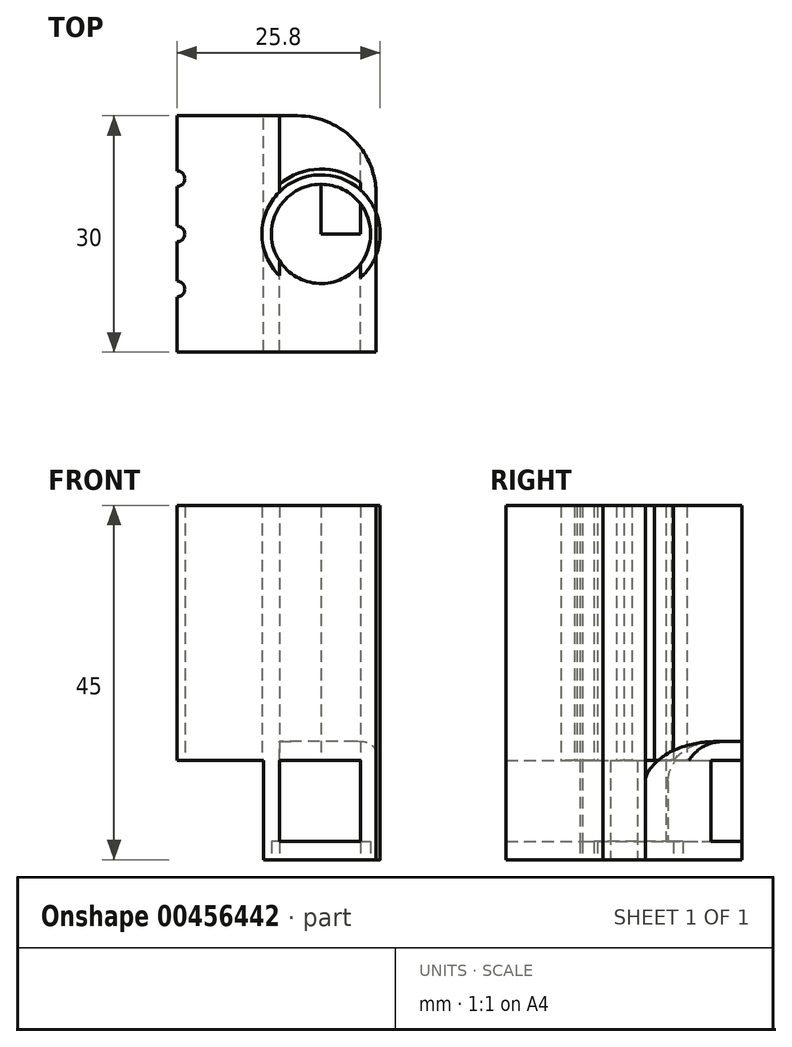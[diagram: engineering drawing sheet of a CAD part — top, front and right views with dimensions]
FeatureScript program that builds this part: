
annotation { "Feature Type Name" : "Feature", "Feature Type Description" : "" }
export const myFeature = defineFeature(function(context is Context, id is Id, definition is map)
    precondition{}
    {
        {
            var Q0;
            Q0=qCreatedBy(makeId("Top.planeOp"),FACE);
            var sketch = newSketch(context, id + "F0", { "sketchPlane" : qUnion([Q0])});
            skLineSegment(sketch, "E0.bottom", {"start": v(0, 0) * mm, "end": v(37, 0) * mm});
            skLineSegment(sketch, "E0.top", {"start": v(0, -30) * mm, "end": v(37, -30) * mm});
            skLineSegment(sketch, "E0.left", {"start": v(0, 0) * mm, "end": v(0, -30) * mm});
            skLineSegment(sketch, "E0.right", {"start": v(37, 0) * mm, "end": v(37, -30) * mm});
            skLineSegment(sketch, "E1.bottom", {"start": v(37, 0) * mm, "end": v(35, 0) * mm});
            skLineSegment(sketch, "E1.top", {"start": v(37, -30) * mm, "end": v(35, -30) * mm});
            skLineSegment(sketch, "E1.right", {"start": v(35, 0) * mm, "end": v(35, -30) * mm});
            skLineSegment(sketch, "E2.bottom", {"start": v(35, 0) * mm, "end": v(24.7, 0) * mm});
            skLineSegment(sketch, "E2.top", {"start": v(35, -30) * mm, "end": v(24.7, -30) * mm});
            skLineSegment(sketch, "E2.right", {"start": v(24.7, 0) * mm, "end": v(24.7, -30) * mm});
            skLineSegment(sketch, "E3.bottom", {"start": v(24.7, 0) * mm, "end": v(11.7, 0) * mm});
            skLineSegment(sketch, "E3.top", {"start": v(24.7, -30) * mm, "end": v(11.7, -30) * mm});
            skLineSegment(sketch, "E3.right", {"start": v(11.7, 0) * mm, "end": v(11.7, -30) * mm});
            skCircle(sketch, "E4", {"center": v(11.7, -15) * mm, "radius": 1 * mm});
            skCircle(sketch, "E5", {"center": v(11.7, -8) * mm, "radius": 1 * mm});
            skCircle(sketch, "E6", {"center": v(11.7, -22) * mm, "radius": 1 * mm});
            skLineSegment(sketch, "E7.bottom", {"start": v(11.7, 0) * mm, "end": v(6.7, 0) * mm});
            skLineSegment(sketch, "E7.top", {"start": v(11.7, -30) * mm, "end": v(6.7, -30) * mm});
            skLineSegment(sketch, "E7.right", {"start": v(6.7, 0) * mm, "end": v(6.7, -30) * mm});
            skCircle(sketch, "E8.MirrorC", {"center": v(1.7, -8) * mm, "radius": 1 * mm});
            skCircle(sketch, "E9.MirrorC", {"center": v(1.7, -15) * mm, "radius": 1 * mm});
            skCircle(sketch, "E10.MirrorC", {"center": v(1.7, -22) * mm, "radius": 1 * mm});
            skCircle(sketch, "E11", {"center": v(30, -15) * mm, "radius": 7.5 * mm});
            skPoint(sketch, "E11.centerSnap0", {"position": v(24.7, -15) * mm});
            skLineSegment(sketch, "E12.bottom", {"start": v(35, 0) * mm, "end": v(30, 0) * mm});
            skLineSegment(sketch, "E12.top", {"start": v(35, -15) * mm, "end": v(30, -15) * mm});
            skLineSegment(sketch, "E12.left", {"start": v(35, 0) * mm, "end": v(35, -15) * mm});
            skLineSegment(sketch, "E12.right", {"start": v(30, 0) * mm, "end": v(30, -15) * mm});
            skCircle(sketch, "E13", {"center": v(30, -15) * mm, "radius": 6.3 * mm});
            skSolve(sketch);
        }
        {
            var Q0;
            {var subQ0=sQuery(id+"F0.wireOp",EDGE,"E1.bottom");Q0=makeQuery(id+"F0.imprint","IMPRINT",FACE,{"disambiguationData":[TD([[makeQuery(id+"F0.imprint","IMPRINT",EDGE,{"derivedFrom":subQ0}),1.0]])]});}
            var Q1;
            {var subQ0=sQuery(id+"F0.wireOp",EDGE,"E1.top");Q1=makeQuery(id+"F0.imprint","IMPRINT",FACE,{"disambiguationData":[TD([[makeQuery(id+"F0.imprint","IMPRINT",EDGE,{"derivedFrom":subQ0}),-1.0]])]});}
            var Q2;
            {var subQ0=sQuery(id+"F0.wireOp",EDGE,"E2.bottom");Q2=makeQuery(id+"F0.imprint","IMPRINT",FACE,{"disambiguationData":[TD([[makeQuery(id+"F0.imprint","IMPRINT",EDGE,{"derivedFrom":subQ0}),1.0]])]});}
            var Q3;
            {var subQ0=sQuery(id+"F0.wireOp",EDGE,"E2.top");Q3=makeQuery(id+"F0.imprint","IMPRINT",FACE,{"disambiguationData":[TD([[makeQuery(id+"F0.imprint","IMPRINT",EDGE,{"derivedFrom":subQ0}),-1.0]])]});}
            var Q4;
            {var subQ5=sQuery(id+"F0.wireOp",EDGE,"E12.bottom");Q4=makeQuery(id+"F0.imprint","IMPRINT",FACE,{"disambiguationData":[TD([[makeQuery(id+"F0.imprint","IMPRINT",EDGE,{"derivedFrom":subQ5}),1.0]])]});}
            var Q5;
            Q5=makeQuery(id+"F0.imprint","IMPRINT",FACE,{"disambiguationData":[TD([[makeQuery(id+"F0.imprint","IMPRINT",EDGE,{"derivedFrom":sQuery(id+"F0.wireOp",EDGE,"E0.bottom")}),-1.0]])]});
            var Q6;
            {var subQ0=sQuery(id+"F0.wireOp",EDGE,"E7.bottom");Q6=makeQuery(id+"F0.imprint","IMPRINT",FACE,{"disambiguationData":[TD([[makeQuery(id+"F0.imprint","IMPRINT",EDGE,{"derivedFrom":subQ0}),1.0]])]});}
            var Q7;
            {var subQ1=sQuery(id+"F0.wireOp",EDGE,"E3.bottom");Q7=makeQuery(id+"F0.imprint","IMPRINT",FACE,{"disambiguationData":[TD([[makeQuery(id+"F0.imprint","IMPRINT",EDGE,{"derivedFrom":subQ1}),1.0]])]});}
            extrude(context, id + "F1", {"entities" : qUnion([Q0, Q1, Q2, Q3, Q4, Q5, Q6, Q7]), "depth" : 15 * mm});
        }
        {
            var Q0;
            {var subQ0=sQuery(id+"F0.wireOp",EDGE,"E12.left");var subQ1=sQuery(id+"F0.wireOp",EDGE,"E11");var subQ2=makeQuery(id+"F0.imprint","INTERSECT",VERTEX,{"derivedFrom":[subQ1,subQ0]});Q0=makeQuery(id+"F0.imprint","IMPRINT",FACE,{"disambiguationData":[TD([[makeQuery(id+"F0.imprint","IMPRINT",EDGE,{"disambiguationData":[TD([[subQ2,-1.0]])],"derivedFrom":subQ1}),1.0]])]});}
            var Q1;
            {var subQ0=sQuery(id+"F0.wireOp",EDGE,"E11");var subQ1=sQuery(id+"F0.wireOp",EDGE,"E2.right");var subQ2=makeQuery(id+"F0.imprint","INTERSECT",VERTEX,{"disambiguationData":[OD(0.0)],"derivedFrom":[subQ1,subQ0]});Q1=makeQuery(id+"F0.imprint","IMPRINT",FACE,{"disambiguationData":[TD([[makeQuery(id+"F0.imprint","IMPRINT",EDGE,{"disambiguationData":[TD([[subQ2,-1.0]])],"derivedFrom":subQ1}),1.0]])]});}
            var Q2;
            {var subQ0=sQuery(id+"F0.wireOp",EDGE,"E11");var subQ1=sQuery(id+"F0.wireOp",EDGE,"E2.right");var subQ2=makeQuery(id+"F0.imprint","INTERSECT",VERTEX,{"disambiguationData":[OD(0.0)],"derivedFrom":[subQ1,subQ0]});Q2=makeQuery(id+"F0.imprint","IMPRINT",FACE,{"disambiguationData":[TD([[makeQuery(id+"F0.imprint","IMPRINT",EDGE,{"disambiguationData":[TD([[subQ2,-1.0]])],"derivedFrom":subQ1}),-1.0]])]});}
            var Q3;
            {var subQ0=sQuery(id+"F0.wireOp",EDGE,"E13");var subQ1=sQuery(id+"F0.wireOp",EDGE,"E1.right");var subQ2=makeQuery(id+"F0.imprint","INTERSECT",VERTEX,{"derivedFrom":[subQ1,subQ0]});Q3=makeQuery(id+"F0.imprint","IMPRINT",FACE,{"disambiguationData":[TD([[makeQuery(id+"F0.imprint","IMPRINT",EDGE,{"disambiguationData":[TD([[subQ2,-1.0]])],"derivedFrom":subQ1}),-1.0]])]});}
            var Q4;
            {var subQ0=sQuery(id+"F0.wireOp",EDGE,"E11");var subQ1=sQuery(id+"F0.wireOp",EDGE,"E0.right");var subQ7=makeQuery(id+"F0.imprint","INTERSECT",VERTEX,{"disambiguationData":[OD(0.0)],"derivedFrom":[subQ1,subQ0]});Q4=makeQuery(id+"F0.imprint","IMPRINT",FACE,{"disambiguationData":[TD([[makeQuery(id+"F0.imprint","IMPRINT",EDGE,{"disambiguationData":[TD([[subQ7,-1.0]])],"derivedFrom":subQ1}),-1.0]])]});}
            extrude(context, id + "F2", {"entities" : qUnion([Q0, Q1, Q2, Q3, Q4]), "operationType" : NewBodyOperationType.ADD, "depth" : 45 * mm});
        }
        {
            var Q0;
            Q0=makeQuery(id+"F1.opExtrude","CAP_EDGE",EDGE,{"disambiguationData":[OSD([sQuery(id+"F0.wireOp",EDGE,"E11")])],"isStart":false});
            fillet(context, id + "F3", {"entities" : qUnion([Q0]), "radius" : 5 * mm, "tangentPropagation" : true, "allowEdgeOverflow" : false});
        }
        {
            var Q0;
            Q0=makeQuery(id+"F1.opExtrude","SWEPT_FACE",FACE,{"disambiguationData":[OSD([sQuery(id+"F0.wireOp",EDGE,"E0.bottom"),sQuery(id+"F0.wireOp",EDGE,"E1.bottom"),sQuery(id+"F0.wireOp",EDGE,"E2.bottom"),sQuery(id+"F0.wireOp",EDGE,"E3.bottom"),sQuery(id+"F0.wireOp",EDGE,"E7.bottom"),sQuery(id+"F0.wireOp",EDGE,"E12.bottom")])]});
            var sketch = newSketch(context, id + "F4", { "sketchPlane" : qUnion([Q0])});
            skLineSegment(sketch, "E14.bottom", {"start": v(-37, 15) * mm, "end": v(-35, 15) * mm});
            skLineSegment(sketch, "E14.top", {"start": v(-37, 12.6) * mm, "end": v(-35, 12.6) * mm});
            skLineSegment(sketch, "E14.left", {"start": v(-37, 15) * mm, "end": v(-37, 12.6) * mm});
            skLineSegment(sketch, "E14.right", {"start": v(-35, 15) * mm, "end": v(-35, 12.6) * mm});
            skLineSegment(sketch, "E15.bottom", {"start": v(-35, 12.6) * mm, "end": v(-24.7, 12.6) * mm});
            skLineSegment(sketch, "E15.top", {"start": v(-35, 2.3) * mm, "end": v(-24.7, 2.3) * mm});
            skLineSegment(sketch, "E15.left", {"start": v(-35, 12.6) * mm, "end": v(-35, 2.3) * mm});
            skLineSegment(sketch, "E15.right", {"start": v(-24.7, 12.6) * mm, "end": v(-24.7, 2.3) * mm});
            skLineSegment(sketch, "E16.bottom", {"start": v(-24.7, 12.6) * mm, "end": v(-22.7, 12.6) * mm});
            skLineSegment(sketch, "E16.top", {"start": v(-24.7, 15) * mm, "end": v(-22.7, 15) * mm});
            skLineSegment(sketch, "E16.left", {"start": v(-24.7, 12.6) * mm, "end": v(-24.7, 15) * mm});
            skLineSegment(sketch, "E16.right", {"start": v(-22.7, 12.6) * mm, "end": v(-22.7, 15) * mm});
            skLineSegment(sketch, "E17.bottom", {"start": v(-22.7, 12.6) * mm, "end": v(0, 12.6) * mm});
            skLineSegment(sketch, "E17.top", {"start": v(-22.7, 0) * mm, "end": v(0, 0) * mm});
            skLineSegment(sketch, "E17.left", {"start": v(-22.7, 12.6) * mm, "end": v(-22.7, 0) * mm});
            skLineSegment(sketch, "E17.right", {"start": v(0, 12.6) * mm, "end": v(0, 0) * mm});
            skSolve(sketch);
        }
        {
            var Q0;
            Q0=makeQuery(id+"F4.imprint","IMPRINT",FACE,{"disambiguationData":[TD([[makeQuery(id+"F4.imprint","IMPRINT",EDGE,{"derivedFrom":sQuery(id+"F4.wireOp",EDGE,"E15.bottom")}),-1.0]])]});
            extrude(context, id + "F5", {"entities" : qUnion([Q0]), "operationType" : NewBodyOperationType.REMOVE, "endBound" : BoundingType.THROUGH_ALL, "oppositeDirection" : true, "depth" : 25 * mm});
        }
        {
            var Q0;
            {var subQ1=sQuery(id+"F0.wireOp",EDGE,"E12.top");Q0=makeQuery(id+"F0.imprint","IMPRINT",FACE,{"disambiguationData":[TD([[makeQuery(id+"F0.imprint","IMPRINT",EDGE,{"derivedFrom":subQ1}),1.0]])]});}
            var Q1;
            {var subQ0=sQuery(id+"F0.wireOp",EDGE,"E12.top");Q1=makeQuery(id+"F0.imprint","IMPRINT",FACE,{"disambiguationData":[TD([[makeQuery(id+"F0.imprint","IMPRINT",EDGE,{"derivedFrom":subQ0}),-1.0]])]});}
            var Q2;
            {var subQ0=sQuery(id+"F0.wireOp",EDGE,"E13");var subQ1=sQuery(id+"F0.wireOp",EDGE,"E2.right");var subQ2=makeQuery(id+"F0.imprint","INTERSECT",VERTEX,{"disambiguationData":[OD(0.0)],"derivedFrom":[subQ1,subQ0]});Q2=makeQuery(id+"F0.imprint","IMPRINT",FACE,{"disambiguationData":[TD([[makeQuery(id+"F0.imprint","IMPRINT",EDGE,{"disambiguationData":[TD([[subQ2,-1.0]])],"derivedFrom":subQ1}),-1.0]])]});}
            var Q3;
            {var subQ1=sQuery(id+"F0.wireOp",EDGE,"E1.right");var subQ3=sQuery(id+"F0.wireOp",EDGE,"E13");var subQ4=makeQuery(id+"F0.imprint","INTERSECT",VERTEX,{"derivedFrom":[subQ1,subQ3]});Q3=makeQuery(id+"F0.imprint","IMPRINT",FACE,{"disambiguationData":[TD([[makeQuery(id+"F0.imprint","IMPRINT",EDGE,{"disambiguationData":[TD([[subQ4,-1.0]])],"derivedFrom":subQ3}),1.0]])]});}
            var Q4;
            Q4=makeQuery(id+"F5.boolean.opBoolean","COPY",FACE,{"disambiguationData":[TD([makeQuery(id+"F1.opExtrude","SWEPT_FACE",FACE,{"disambiguationData":[OSD([sQuery(id+"F0.wireOp",EDGE,"E0.bottom"),sQuery(id+"F0.wireOp",EDGE,"E1.bottom"),sQuery(id+"F0.wireOp",EDGE,"E2.bottom"),sQuery(id+"F0.wireOp",EDGE,"E3.bottom"),sQuery(id+"F0.wireOp",EDGE,"E7.bottom"),sQuery(id+"F0.wireOp",EDGE,"E12.bottom")])]})])],"derivedFrom":makeQuery(id+"F5.opExtrude","SWEPT_FACE",FACE,{"disambiguationData":[OSD([sQuery(id+"F4.wireOp",EDGE,"E15.top")])]})});
            extrude(context, id + "F6", {"entities" : qUnion([Q0, Q1, Q2, Q3]), "operationType" : NewBodyOperationType.ADD, "endBound" : BoundingType.UP_TO_SURFACE, "endBoundEntityFace" : qUnion([Q4]), "depth" : 25 * mm});
        }
        {
            var Q0;
            Q0=makeQuery(id+"F4.imprint","IMPRINT",FACE,{"disambiguationData":[TD([[makeQuery(id+"F4.imprint","IMPRINT",EDGE,{"derivedFrom":sQuery(id+"F4.wireOp",EDGE,"E17.bottom")}),-1.0]])]});
            extrude(context, id + "F7", {"entities" : qUnion([Q0]), "operationType" : NewBodyOperationType.REMOVE, "endBound" : BoundingType.THROUGH_ALL, "oppositeDirection" : true, "depth" : 25 * mm});
        }
        {
            var Q0;
            Q0=makeQuery(id+"F1.opExtrude","SWEPT_EDGE",EDGE,{"disambiguationData":[OSD([sQuery(id+"F0.wireOp",EDGE,"E0.top"),sQuery(id+"F0.wireOp",EDGE,"E0.left")])]});
            var Q1;
            Q1=makeQuery(id+"F1.opExtrude","SWEPT_EDGE",EDGE,{"disambiguationData":[OSD([sQuery(id+"F0.wireOp",EDGE,"E0.bottom"),sQuery(id+"F0.wireOp",EDGE,"E0.left")])]});
            fillet(context, id + "F8", {"entities" : qUnion([Q0, Q1]), "radius" : 10 * mm, "tangentPropagation" : true, "allowEdgeOverflow" : false});
        }
    });
